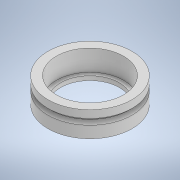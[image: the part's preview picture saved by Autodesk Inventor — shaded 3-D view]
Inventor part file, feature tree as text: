
AUTODESK INVENTOR PART (.ipt)
format: ipt  version: 2022.2 (Build 262287000, 287)  size: 130,048 bytes
history: native  units: mm
features: revolve x1, sketch x1
ambient origin geometry x8: Origin, YZ Plane, XZ Plane, XY Plane, X Axis, Y Axis, Z Axis, Center Point
bodies: Solid1 (feature_tree)
feature tree (2):
  revolve  "Revolution1"  [1 undecoded]
  sketch  "Sketch2"  dims[d1=1.0mm d2=1.0mm d3=5.0mm d4=1.0mm d5=8.0mm d6=2.0mm d7=2.0mm d8=90.0deg]
note: 1 required parameter value undecoded (feature->parameter linkage not recoverable at this tier; creation-order binding heuristic only, values carry confidence <= 0.55)
